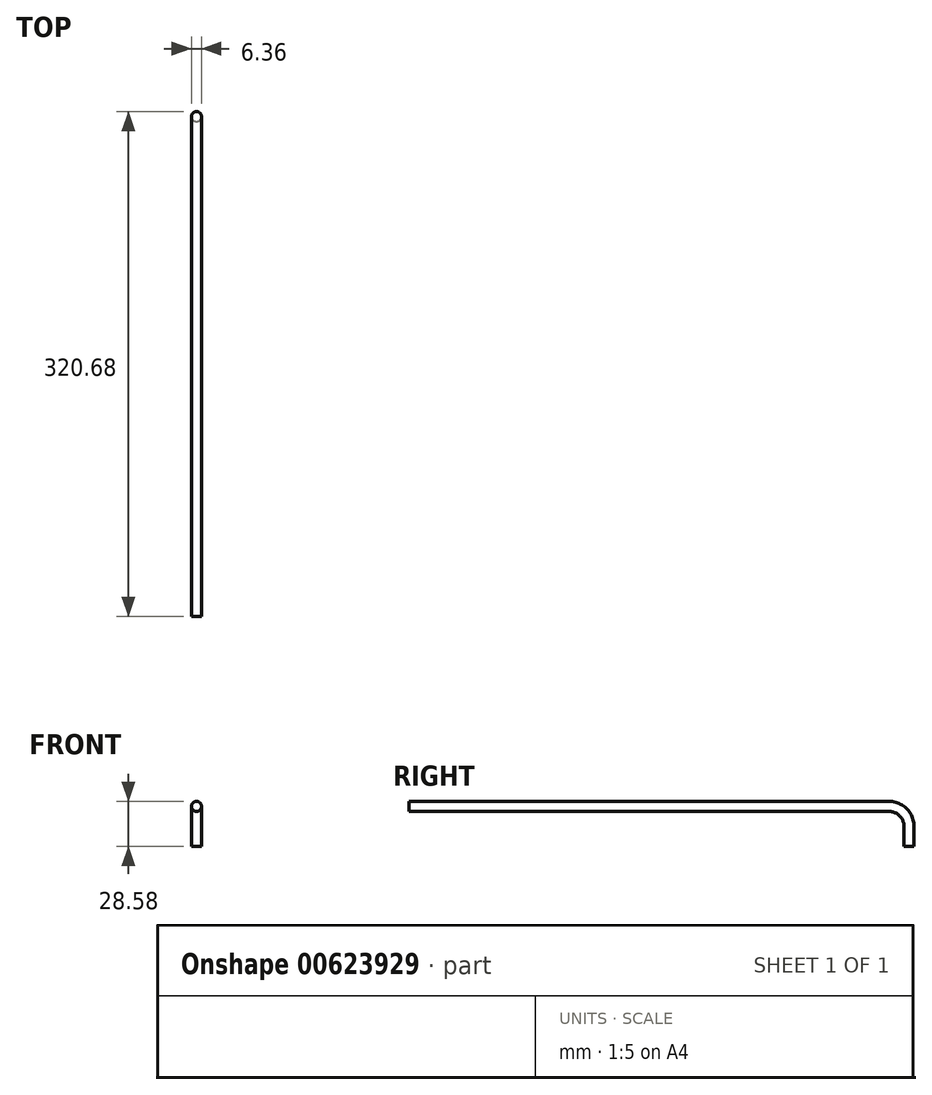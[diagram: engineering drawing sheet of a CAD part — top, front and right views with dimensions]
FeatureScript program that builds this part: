
annotation { "Feature Type Name" : "Feature", "Feature Type Description" : "" }
export const myFeature = defineFeature(function(context is Context, id is Id, definition is map)
    precondition{}
    {
        {
            var Q0;
            Q0=qCreatedBy(makeId("Front.planeOp"),FACE);
            var sketch = newSketch(context, id + "F0", { "sketchPlane" : qUnion([Q0])});
            skCircle(sketch, "E0", {"center": v(0, 0) * mm, "radius": 3.18 * mm});
            skSolve(sketch);
        }
        {
            var Q0;
            Q0=qSketchRegion(id+"F0",true);
            extrude(context, id + "F1", {"entities" : qUnion([Q0]), "depth" : 304.8 * mm});
        }
        {
            var Q0;
            Q0=qCreatedBy(makeId("Right.planeOp"),FACE);
            var sketch = newSketch(context, id + "F2", { "sketchPlane" : qUnion([Q0])});
            skArc(sketch, "E1", {"start": v(12.7, -12.7) * mm, "mid": v(8.98, -3.72) * mm, "end": v(0, 0) * mm});
            skLineSegment(sketch, "E2", {"start": v(51.54, 0) * mm, "end": v(0, 0) * mm, "construction": true});
            skLineSegment(sketch, "E3", {"start": v(12.7, -12.7) * mm, "end": v(12.7, -25.4) * mm});
            skSolve(sketch);
        }
        {
            var Q0;
            Q0=makeQuery(id+"F1.opExtrude","CAP_FACE",FACE,{"disambiguationData":[OSD([sQuery(id+"F0.wireOp",EDGE,"E0")])],"isStart":true});
            var Q1;
            Q1=sQuery(id+"F2.wireOp",EDGE,"E1");
            var Q2;
            Q2=sQuery(id+"F2.wireOp",EDGE,"E3");
            sweep(context, id + "F3", {"operationType" : NewBodyOperationType.ADD, "profiles" : qUnion([Q0]), "path" : qUnion([Q1, Q2])});
        }
    });
